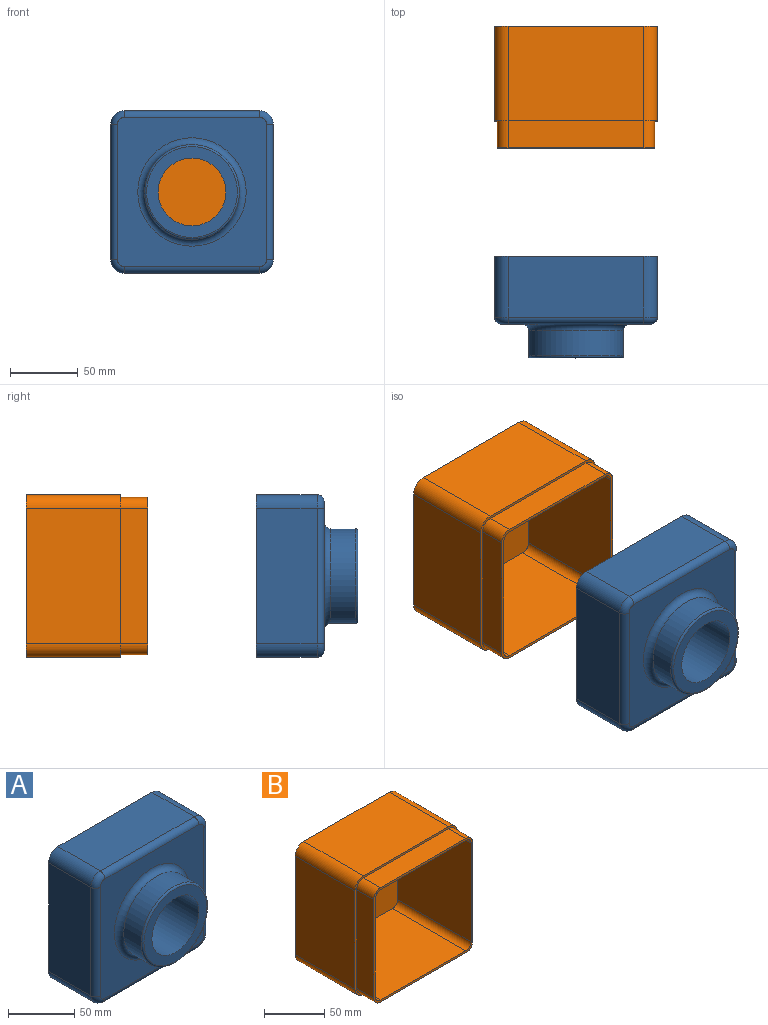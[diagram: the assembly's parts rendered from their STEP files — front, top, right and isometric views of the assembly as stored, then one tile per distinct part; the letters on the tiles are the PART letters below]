
ASSEMBLY  parts=2 mates=1
PART A: 45 faces, bbox 121.6x75x121.6 mm
  f0: plane 120x120mm, normal (0,1,0), area 913.1mm2, adj f1,f2,f3,f4,f10,f11,f12,f13
  f1: plane 100x45mm, normal (-1,0,0), area 4500mm2, adj f0,f10,f13,f19
  f2: plane 100x45mm, normal (0,0,-1), area 4500mm2, adj f0,f10,f11,f20
  f3: plane 100x45mm, normal (1,0,0), area 4500mm2, adj f0,f11,f12,f16
  f4: plane 100x45mm, normal (0,0,1), area 4500mm2, adj f0,f12,f13,f15
  f5: plane 110x110mm, normal (0,-1,0), area 7052mm2, adj f14,f15,f16,f17,f18,f19,f20,f21
  f6: plane 54x54mm, normal (0,1,0), area 326.7mm2, adj f9,f31
  f7: cylinder r=35mm len=70mm, axis (0,1,0), area 4068.4mm2, adj f22,f23
  f8: plane 67x67mm, normal (0,-1,0), area 1562.2mm2, adj f9,f23
  f9: cylinder r=25mm len=75mm, axis (0,-1,0), area 11781mm2, adj f6,f8
  f10: cylinder r=10mm len=45mm, axis (0,-1,0), area 706.9mm2, adj f0,f1,f2,f21
  f11: cylinder r=10mm len=45mm, axis (0,1,0), area 706.9mm2, adj f0,f2,f3,f18
  f12: cylinder r=10mm len=45mm, axis (0,-1,0), area 706.9mm2, adj f0,f3,f4,f14
  f13: cylinder r=10mm len=45mm, axis (0,1,0), area 706.9mm2, adj f0,f1,f4,f17
  f14: torus R=5mm, axis (0,-1,0), area 101mm2, adj f5,f12,f15,f16
  f15: cylinder r=5mm len=100mm, axis (1,0,0), area 785.4mm2, adj f4,f5,f14,f17
  f16: cylinder r=5mm len=100mm, axis (0,0,-1), area 785.4mm2, adj f3,f5,f14,f18
  f17: torus R=5mm, axis (0,-1,0), area 101mm2, adj f5,f13,f15,f19
  f18: torus R=5mm, axis (0,-1,0), area 101mm2, adj f5,f11,f16,f20
  f19: cylinder r=5mm len=100mm, axis (0,0,1), area 785.4mm2, adj f1,f5,f17,f21
  f20: cylinder r=5mm len=100mm, axis (-1,0,0), area 785.4mm2, adj f2,f5,f18,f21
  f21: torus R=5mm, axis (0,-1,0), area 101mm2, adj f5,f10,f19,f20
  f22: torus R=40mm, axis (0,-1,0), area 1816.8mm2, adj f5,f7
  f23: torus R=33.5mm, axis (0,-1,0), area 510.1mm2, adj f7,f8
  f24: plane 100x45mm, normal (1,0,0), area 4500mm2, adj f0,f32,f35,f41
  f25: plane 100x45mm, normal (0,0,1), area 4500mm2, adj f0,f32,f33,f42
  f26: plane 100x45mm, normal (-1,0,0), area 4500mm2, adj f0,f33,f34,f38
  f27: plane 100x45mm, normal (0,0,-1), area 4500mm2, adj f0,f34,f35,f37
  f28: plane 110x110mm, normal (0,1,0), area 7052mm2, adj f36,f37,f38,f39,f40,f41,f42,f43
  f29: cylinder r=33mm len=66mm, axis (0,1,0), area 3732.2mm2, adj f30,f44
  f30: plane 66x66mm, normal (0,1,0), area 1131mm2, adj f29,f31
  f31: cylinder r=27mm len=73mm, axis (0,-1,0), area 12384.2mm2, adj f6,f30
  f32: cylinder r=8mm len=45mm, axis (0,-1,0), area 565.5mm2, adj f0,f24,f25,f43
  f33: cylinder r=8mm len=45mm, axis (0,1,0), area 565.5mm2, adj f0,f25,f26,f40
  f34: cylinder r=8mm len=45mm, axis (0,-1,0), area 565.5mm2, adj f0,f26,f27,f36
  f35: cylinder r=8mm len=45mm, axis (0,1,0), area 565.5mm2, adj f0,f24,f27,f39
  f36: torus R=5mm, axis (0,-1,0), area 51.1mm2, adj f28,f34,f37,f38
  f37: cylinder r=3mm len=100mm, axis (1,0,0), area 471.2mm2, adj f27,f28,f36,f39
  f38: cylinder r=3mm len=100mm, axis (0,0,-1), area 471.2mm2, adj f26,f28,f36,f40
  f39: torus R=5mm, axis (0,-1,0), area 51.1mm2, adj f28,f35,f37,f41
  f40: torus R=5mm, axis (0,-1,0), area 51.1mm2, adj f28,f33,f38,f42
  f41: cylinder r=3mm len=100mm, axis (0,0,1), area 471.2mm2, adj f24,f28,f39,f43
  f42: cylinder r=3mm len=100mm, axis (-1,0,0), area 471.2mm2, adj f25,f28,f40,f43
  f43: torus R=5mm, axis (0,-1,0), area 51.1mm2, adj f28,f32,f41,f42
  f44: torus R=40mm, axis (0,-1,0), area 2455.6mm2, adj f28,f29
PART B: 28 faces, bbox 120x90x120 mm
  f0: plane 116x116mm, normal (0,-1,0), area 888mm2, adj f1,f2,f3,f4,f6,f7,f8,f9
  f1: plane 100x86mm, normal (1,0,0), area 8600mm2, adj f0,f5,f6,f9
  f2: plane 100x86mm, normal (0,0,1), area 8600mm2, adj f0,f5,f6,f7
  f3: plane 100x86mm, normal (-1,0,0), area 8600mm2, adj f0,f5,f7,f8
  f4: plane 100x86mm, normal (0,0,-1), area 8600mm2, adj f0,f5,f8,f9
  f5: plane 112x112mm, normal (0,-1,0), area 12513.1mm2, adj f1,f2,f3,f4,f6,f7,f8,f9
  f6: cylinder r=6mm len=86mm, axis (0,-1,0), area 810.5mm2, adj f0,f1,f2,f5
  f7: cylinder r=6mm len=86mm, axis (0,1,0), area 810.5mm2, adj f0,f2,f3,f5
  f8: cylinder r=6mm len=86mm, axis (0,-1,0), area 810.5mm2, adj f0,f3,f4,f5
  f9: cylinder r=6mm len=86mm, axis (0,1,0), area 810.5mm2, adj f0,f1,f4,f5
  f10: cylinder r=8mm len=20mm, axis (0,-1,0), area 251.3mm2, adj f0,f11,f17,f18
  f11: plane 100x20mm, normal (-1,0,0), area 2000mm2, adj f0,f10,f12,f18
  f12: cylinder r=8mm len=20mm, axis (0,-1,0), area 251.3mm2, adj f0,f11,f13,f18
  f13: plane 100x20mm, normal (0,0,1), area 2000mm2, adj f0,f12,f14,f18
  f14: cylinder r=8mm len=20mm, axis (0,-1,0), area 251.3mm2, adj f0,f13,f15,f18
  f15: plane 100x20mm, normal (1,0,0), area 2000mm2, adj f0,f14,f16,f18
  f16: cylinder r=8mm len=20mm, axis (0,-1,0), area 251.3mm2, adj f0,f15,f17,f18
  f17: plane 100x20mm, normal (0,0,-1), area 2000mm2, adj f0,f10,f16,f18
  f18: plane 120x120mm, normal (0,-1,0), area 913.1mm2, adj f10,f11,f12,f13,f14,f15,f16,f17
  f19: plane 120x120mm, normal (0,1,0), area 14314.2mm2, adj f20,f21,f22,f23,f24,f25,f26,f27
  f20: cylinder r=10mm len=70mm, axis (0,-1,0), area 1099.6mm2, adj f18,f19,f22,f24
  f21: cylinder r=10mm len=70mm, axis (0,1,0), area 1099.6mm2, adj f18,f19,f22,f27
  f22: plane 100x70mm, normal (0,0,1), area 7000mm2, adj f18,f19,f20,f21
  f23: cylinder r=10mm len=70mm, axis (0,1,0), area 1099.6mm2, adj f18,f19,f24,f26
  f24: plane 100x70mm, normal (1,0,0), area 7000mm2, adj f18,f19,f20,f23
  f25: cylinder r=10mm len=70mm, axis (0,-1,0), area 1099.6mm2, adj f18,f19,f26,f27
  f26: plane 100x70mm, normal (0,0,-1), area 7000mm2, adj f18,f19,f23,f25
  f27: plane 100x70mm, normal (-1,0,0), area 7000mm2, adj f18,f19,f21,f25
PLACE A t=(-73.14,-39.56,-135.19)mm fixed
PLACE B rot(axis=(1,0,0),0deg) t=(-73.14,130.44,-135.19)mm
MATE slider A.f7 <-> B.f18  axis (0,1,0) through (-13.14,-39.56,-75.19)mm
